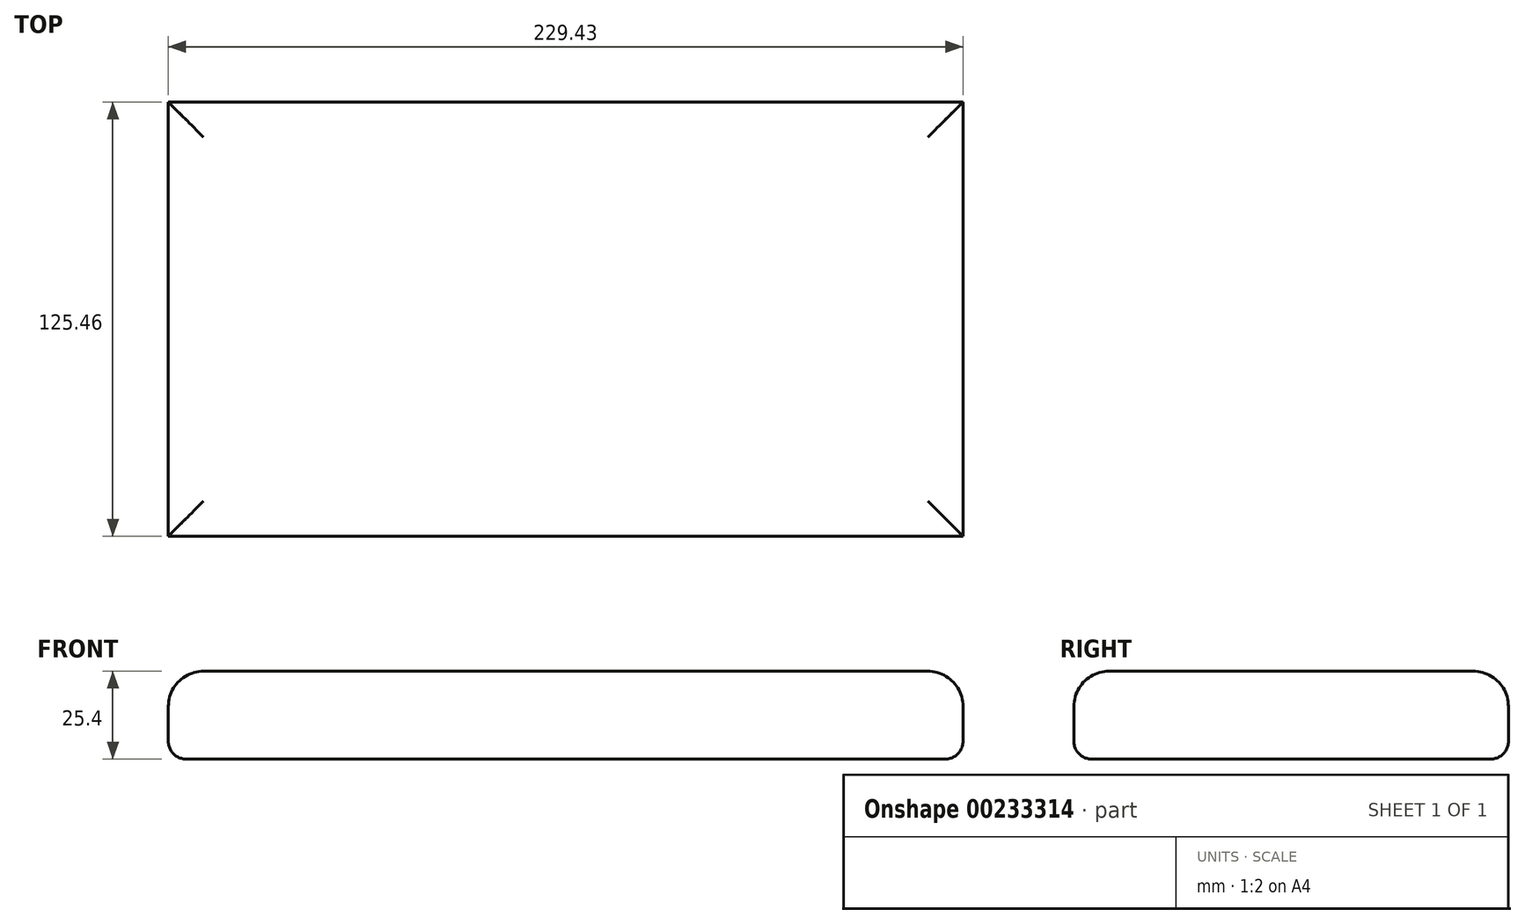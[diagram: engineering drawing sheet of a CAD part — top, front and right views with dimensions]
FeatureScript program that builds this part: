
annotation { "Feature Type Name" : "Feature", "Feature Type Description" : "" }
export const myFeature = defineFeature(function(context is Context, id is Id, definition is map)
    precondition{}
    {
        {
            var Q0;
            Q0=qCreatedBy(makeId("Top.planeOp"),FACE);
            var sketch = newSketch(context, id + "F0", { "sketchPlane" : qUnion([Q0])});
            skLineSegment(sketch, "E0.bottom", {"start": v(-111.23, 55.32) * mm, "end": v(118.2, 55.32) * mm});
            skLineSegment(sketch, "E0.top", {"start": v(-111.23, -70.14) * mm, "end": v(118.2, -70.14) * mm});
            skLineSegment(sketch, "E0.left", {"start": v(-111.23, 55.32) * mm, "end": v(-111.23, -70.14) * mm});
            skLineSegment(sketch, "E0.right", {"start": v(118.2, 55.32) * mm, "end": v(118.2, -70.14) * mm});
            skSolve(sketch);
        }
        {
            var Q0;
            Q0=makeQuery(id+"F0.imprint","IMPRINT",FACE,{"disambiguationData":[TD([[makeQuery(id+"F0.imprint","IMPRINT",EDGE,{"derivedFrom":sQuery(id+"F0.wireOp",EDGE,"E0.bottom")}),-1.0]])]});
            extrude(context, id + "F1", {"entities" : qUnion([Q0]), "depth" : 25.4 * mm});
        }
        {
            var Q0;
            Q0=makeQuery(id+"F1.opExtrude","CAP_FACE",FACE,{"disambiguationData":[OSD([sQuery(id+"F0.wireOp",EDGE,"E0.bottom"),sQuery(id+"F0.wireOp",EDGE,"E0.top"),sQuery(id+"F0.wireOp",EDGE,"E0.left"),sQuery(id+"F0.wireOp",EDGE,"E0.right")])],"isStart":false});
            fillet(context, id + "F2", {"entities" : qUnion([Q0]), "radius" : 10.16 * mm, "tangentPropagation" : true, "allowEdgeOverflow" : false});
        }
        {
            var Q0;
            Q0=makeQuery(id+"F1.opExtrude","CAP_FACE",FACE,{"disambiguationData":[OSD([sQuery(id+"F0.wireOp",EDGE,"E0.bottom"),sQuery(id+"F0.wireOp",EDGE,"E0.top"),sQuery(id+"F0.wireOp",EDGE,"E0.left"),sQuery(id+"F0.wireOp",EDGE,"E0.right")])],"isStart":true});
            fillet(context, id + "F3", {"entities" : qUnion([Q0]), "radius" : 5.08 * mm, "tangentPropagation" : true, "allowEdgeOverflow" : false});
        }
    });
